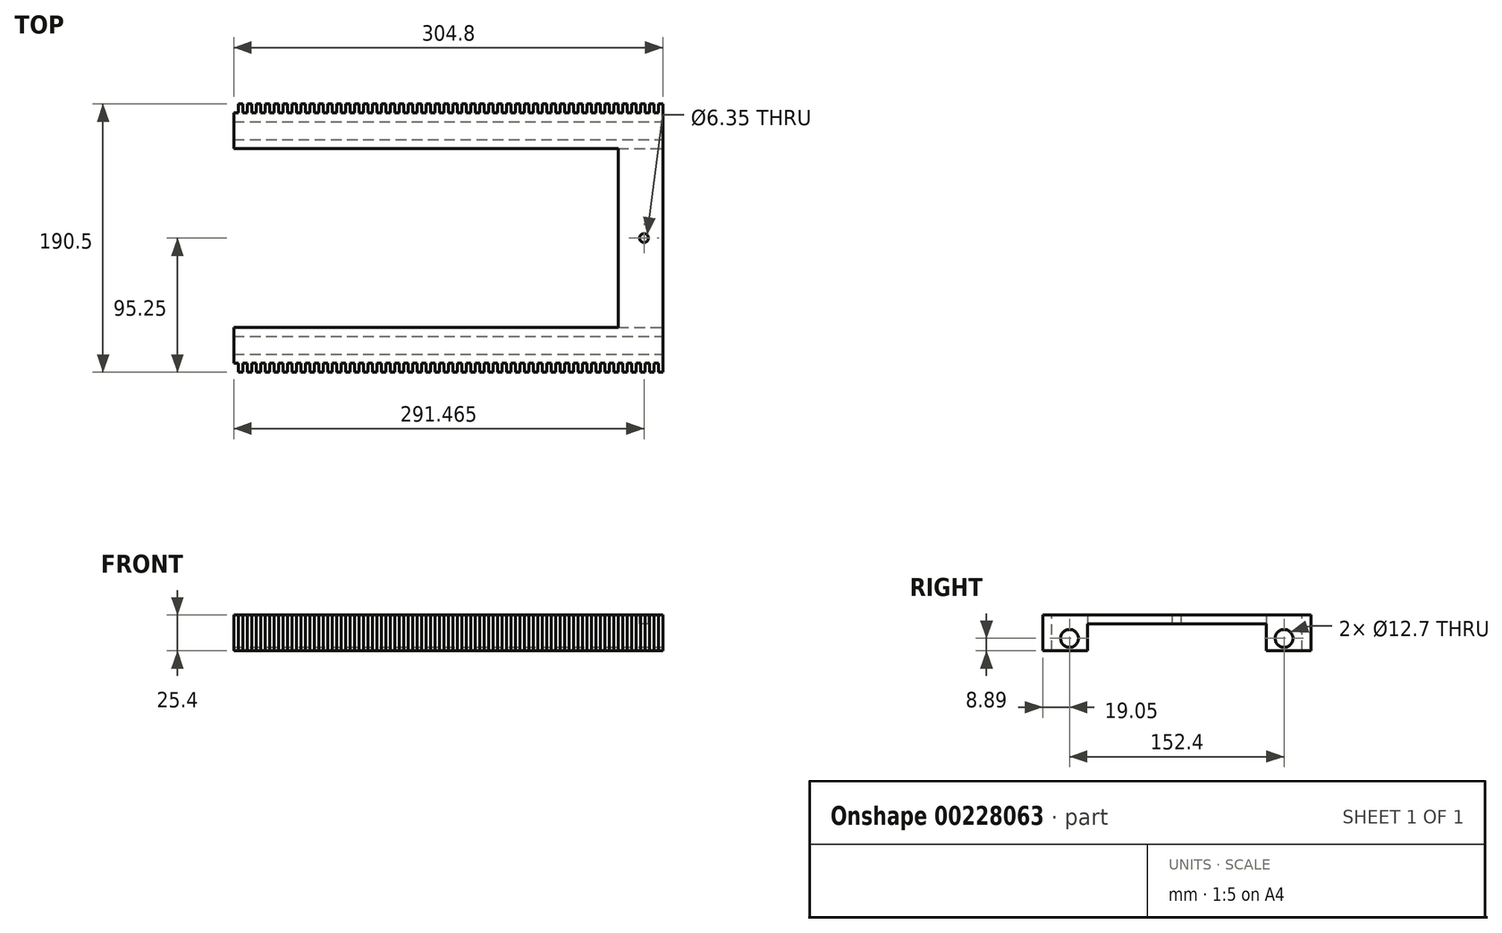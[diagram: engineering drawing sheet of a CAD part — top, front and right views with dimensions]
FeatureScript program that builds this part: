
annotation { "Feature Type Name" : "Feature", "Feature Type Description" : "" }
export const myFeature = defineFeature(function(context is Context, id is Id, definition is map)
    precondition{}
    {
        {
            var Q0;
            Q0=qCreatedBy(makeId("Top.planeOp"),FACE);
            var sketch = newSketch(context, id + "F0", { "sketchPlane" : qUnion([Q0])});
            skLineSegment(sketch, "E0.bottom", {"start": v(0, 0) * mm, "end": v(304.8, 0) * mm});
            skLineSegment(sketch, "E0.top", {"start": v(0, 190.5) * mm, "end": v(304.8, 190.5) * mm});
            skLineSegment(sketch, "E0.left", {"start": v(0, 0) * mm, "end": v(0, 190.5) * mm});
            skLineSegment(sketch, "E0.right", {"start": v(304.8, 0) * mm, "end": v(304.8, 190.5) * mm});
            skLineSegment(sketch, "E1.bottom", {"start": v(6.35, 158.75) * mm, "end": v(273.05, 158.75) * mm});
            skLineSegment(sketch, "E1.top", {"start": v(6.35, 31.75) * mm, "end": v(273.05, 31.75) * mm});
            skLineSegment(sketch, "E1.left", {"start": v(6.35, 158.75) * mm, "end": v(6.35, 31.75) * mm});
            skLineSegment(sketch, "E1.right", {"start": v(273.05, 158.75) * mm, "end": v(273.05, 31.75) * mm});
            skLineSegment(sketch, "E2", {"start": v(0, 190.5) * mm, "end": v(6.35, 158.75) * mm, "construction": true});
            skLineSegment(sketch, "E3", {"start": v(6.35, 31.75) * mm, "end": v(0, 0) * mm, "construction": true});
            skSolve(sketch);
        }
        {
            var Q0;
            Q0 = qSketchRegion(id + "F0", true);
            extrude(context, id + "F1", {"entities" : qUnion([Q0]), "depth" : 6.35 * mm, "offsetDistance" : 25.4 * mm});
        }
        {
            var Q0;
            Q0=makeQuery(id+"F1.opExtrude","SWEPT_FACE",FACE,{"disambiguationData":[OSD([sQuery(id+"F0.wireOp",EDGE,"E0.right")])]});
            var sketch = newSketch(context, id + "F2", { "sketchPlane" : qUnion([Q0])});
            skLineSegment(sketch, "E4.bottom", {"start": v(0, 0) * mm, "end": v(31.75, 0) * mm});
            skLineSegment(sketch, "E4.top", {"start": v(0, -19.05) * mm, "end": v(31.75, -19.05) * mm});
            skLineSegment(sketch, "E4.left", {"start": v(0, 0) * mm, "end": v(0, -19.05) * mm});
            skLineSegment(sketch, "E4.right", {"start": v(31.75, 0) * mm, "end": v(31.75, -19.05) * mm});
            skLineSegment(sketch, "E5.bottom", {"start": v(190.5, 0) * mm, "end": v(158.75, 0) * mm});
            skLineSegment(sketch, "E5.top", {"start": v(190.5, -19.05) * mm, "end": v(158.75, -19.05) * mm});
            skLineSegment(sketch, "E5.left", {"start": v(190.5, 0) * mm, "end": v(190.5, -19.05) * mm});
            skLineSegment(sketch, "E5.right", {"start": v(158.75, 0) * mm, "end": v(158.75, -19.05) * mm});
            skCircle(sketch, "E6", {"center": v(19.05, -10.16) * mm, "radius": 6.35 * mm});
            skCircle(sketch, "E7", {"center": v(171.45, -10.16) * mm, "radius": 6.35 * mm});
            skLineSegment(sketch, "E8", {"start": v(19.05, -10.16) * mm, "end": v(0, 0) * mm, "construction": true});
            skLineSegment(sketch, "E9", {"start": v(171.45, -10.16) * mm, "end": v(190.5, 0) * mm, "construction": true});
            skSolve(sketch);
        }
        {
            var Q0;
            Q0 = qSketchRegion(id + "F2", true);
            var Q1;
            Q1=makeQuery(id+"F1.opExtrude","SWEPT_FACE",FACE,{"disambiguationData":[OSD([sQuery(id+"F0.wireOp",EDGE,"E0.left")])]});
            extrude(context, id + "F3", {"entities" : qUnion([Q0]), "operationType" : NewBodyOperationType.ADD, "endBound" : BoundingType.UP_TO_SURFACE, "oppositeDirection" : true, "depth" : 25.4 * mm, "endBoundEntityFace" : qUnion([Q1]), "offsetDistance" : 25.4 * mm});
        }
        {
            var Q0;
            Q0=makeQuery(id+"F1.opExtrude","CAP_FACE",FACE,{"disambiguationData":[OSD([sQuery(id+"F0.wireOp",EDGE,"E0.bottom"),sQuery(id+"F0.wireOp",EDGE,"E0.top"),sQuery(id+"F0.wireOp",EDGE,"E0.left"),sQuery(id+"F0.wireOp",EDGE,"E0.right"),sQuery(id+"F0.wireOp",EDGE,"E1.bottom"),sQuery(id+"F0.wireOp",EDGE,"E1.top"),sQuery(id+"F0.wireOp",EDGE,"E1.left"),sQuery(id+"F0.wireOp",EDGE,"E1.right")])],"isStart":false});
            var sketch = newSketch(context, id + "F4", { "sketchPlane" : qUnion([Q0])});
            skLineSegment(sketch, "E10.bottom", {"start": v(0, 190.5) * mm, "end": v(3.18, 190.5) * mm});
            skLineSegment(sketch, "E10.top", {"start": v(0, 184.15) * mm, "end": v(3.18, 184.15) * mm});
            skLineSegment(sketch, "E10.left", {"start": v(0, 190.5) * mm, "end": v(0, 184.15) * mm});
            skLineSegment(sketch, "E10.right", {"start": v(3.18, 190.5) * mm, "end": v(3.18, 184.15) * mm});
            skLineSegment(sketch, "E11", {"start": v(0, 95.25) * mm, "end": v(304.8, 95.25) * mm, "construction": true});
            skLineSegment(sketch, "E12.1.0.0", {"start": v(6.35, 190.5) * mm, "end": v(9.53, 190.5) * mm});
            skLineSegment(sketch, "E12.1.0.1", {"start": v(6.35, 184.15) * mm, "end": v(9.53, 184.15) * mm});
            skLineSegment(sketch, "E12.1.0.2", {"start": v(6.35, 190.5) * mm, "end": v(6.35, 184.15) * mm});
            skLineSegment(sketch, "E12.1.0.3", {"start": v(9.53, 190.5) * mm, "end": v(9.53, 184.15) * mm});
            skLineSegment(sketch, "E12.2.0.0", {"start": v(12.7, 190.5) * mm, "end": v(15.88, 190.5) * mm});
            skLineSegment(sketch, "E12.2.0.1", {"start": v(12.7, 184.15) * mm, "end": v(15.88, 184.15) * mm});
            skLineSegment(sketch, "E12.2.0.2", {"start": v(12.7, 190.5) * mm, "end": v(12.7, 184.15) * mm});
            skLineSegment(sketch, "E12.2.0.3", {"start": v(15.88, 190.5) * mm, "end": v(15.88, 184.15) * mm});
            skLineSegment(sketch, "E12.3.0.0", {"start": v(19.05, 190.5) * mm, "end": v(22.23, 190.5) * mm});
            skLineSegment(sketch, "E12.3.0.1", {"start": v(19.05, 184.15) * mm, "end": v(22.23, 184.15) * mm});
            skLineSegment(sketch, "E12.3.0.2", {"start": v(19.05, 190.5) * mm, "end": v(19.05, 184.15) * mm});
            skLineSegment(sketch, "E12.3.0.3", {"start": v(22.23, 190.5) * mm, "end": v(22.23, 184.15) * mm});
            skLineSegment(sketch, "E12.4.0.0", {"start": v(25.4, 190.5) * mm, "end": v(28.58, 190.5) * mm});
            skLineSegment(sketch, "E12.4.0.1", {"start": v(25.4, 184.15) * mm, "end": v(28.58, 184.15) * mm});
            skLineSegment(sketch, "E12.4.0.2", {"start": v(25.4, 190.5) * mm, "end": v(25.4, 184.15) * mm});
            skLineSegment(sketch, "E12.4.0.3", {"start": v(28.58, 190.5) * mm, "end": v(28.58, 184.15) * mm});
            skLineSegment(sketch, "E12.5.0.0", {"start": v(31.75, 190.5) * mm, "end": v(34.93, 190.5) * mm});
            skLineSegment(sketch, "E12.5.0.1", {"start": v(31.75, 184.15) * mm, "end": v(34.93, 184.15) * mm});
            skLineSegment(sketch, "E12.5.0.2", {"start": v(31.75, 190.5) * mm, "end": v(31.75, 184.15) * mm});
            skLineSegment(sketch, "E12.5.0.3", {"start": v(34.93, 190.5) * mm, "end": v(34.93, 184.15) * mm});
            skLineSegment(sketch, "E12.6.0.0", {"start": v(38.1, 190.5) * mm, "end": v(41.28, 190.5) * mm});
            skLineSegment(sketch, "E12.6.0.1", {"start": v(38.1, 184.15) * mm, "end": v(41.28, 184.15) * mm});
            skLineSegment(sketch, "E12.6.0.2", {"start": v(38.1, 190.5) * mm, "end": v(38.1, 184.15) * mm});
            skLineSegment(sketch, "E12.6.0.3", {"start": v(41.28, 190.5) * mm, "end": v(41.28, 184.15) * mm});
            skLineSegment(sketch, "E12.7.0.0", {"start": v(44.45, 190.5) * mm, "end": v(47.63, 190.5) * mm});
            skLineSegment(sketch, "E12.7.0.1", {"start": v(44.45, 184.15) * mm, "end": v(47.63, 184.15) * mm});
            skLineSegment(sketch, "E12.7.0.2", {"start": v(44.45, 190.5) * mm, "end": v(44.45, 184.15) * mm});
            skLineSegment(sketch, "E12.7.0.3", {"start": v(47.63, 190.5) * mm, "end": v(47.63, 184.15) * mm});
            skLineSegment(sketch, "E12.8.0.0", {"start": v(50.8, 190.5) * mm, "end": v(53.98, 190.5) * mm});
            skLineSegment(sketch, "E12.8.0.1", {"start": v(50.8, 184.15) * mm, "end": v(53.98, 184.15) * mm});
            skLineSegment(sketch, "E12.8.0.2", {"start": v(50.8, 190.5) * mm, "end": v(50.8, 184.15) * mm});
            skLineSegment(sketch, "E12.8.0.3", {"start": v(53.98, 190.5) * mm, "end": v(53.98, 184.15) * mm});
            skLineSegment(sketch, "E12.9.0.0", {"start": v(57.15, 190.5) * mm, "end": v(60.33, 190.5) * mm});
            skLineSegment(sketch, "E12.9.0.1", {"start": v(57.15, 184.15) * mm, "end": v(60.33, 184.15) * mm});
            skLineSegment(sketch, "E12.9.0.2", {"start": v(57.15, 190.5) * mm, "end": v(57.15, 184.15) * mm});
            skLineSegment(sketch, "E12.9.0.3", {"start": v(60.33, 190.5) * mm, "end": v(60.33, 184.15) * mm});
            skLineSegment(sketch, "E12.10.0.0", {"start": v(63.5, 190.5) * mm, "end": v(66.68, 190.5) * mm});
            skLineSegment(sketch, "E12.10.0.1", {"start": v(63.5, 184.15) * mm, "end": v(66.68, 184.15) * mm});
            skLineSegment(sketch, "E12.10.0.2", {"start": v(63.5, 190.5) * mm, "end": v(63.5, 184.15) * mm});
            skLineSegment(sketch, "E12.10.0.3", {"start": v(66.68, 190.5) * mm, "end": v(66.68, 184.15) * mm});
            skLineSegment(sketch, "E12.11.0.0", {"start": v(69.85, 190.5) * mm, "end": v(73.03, 190.5) * mm});
            skLineSegment(sketch, "E12.11.0.1", {"start": v(69.85, 184.15) * mm, "end": v(73.03, 184.15) * mm});
            skLineSegment(sketch, "E12.11.0.2", {"start": v(69.85, 190.5) * mm, "end": v(69.85, 184.15) * mm});
            skLineSegment(sketch, "E12.11.0.3", {"start": v(73.03, 190.5) * mm, "end": v(73.03, 184.15) * mm});
            skLineSegment(sketch, "E12.12.0.0", {"start": v(76.2, 190.5) * mm, "end": v(79.38, 190.5) * mm});
            skLineSegment(sketch, "E12.12.0.1", {"start": v(76.2, 184.15) * mm, "end": v(79.38, 184.15) * mm});
            skLineSegment(sketch, "E12.12.0.2", {"start": v(76.2, 190.5) * mm, "end": v(76.2, 184.15) * mm});
            skLineSegment(sketch, "E12.12.0.3", {"start": v(79.38, 190.5) * mm, "end": v(79.38, 184.15) * mm});
            skLineSegment(sketch, "E12.13.0.0", {"start": v(82.55, 190.5) * mm, "end": v(85.73, 190.5) * mm});
            skLineSegment(sketch, "E12.13.0.1", {"start": v(82.55, 184.15) * mm, "end": v(85.73, 184.15) * mm});
            skLineSegment(sketch, "E12.13.0.2", {"start": v(82.55, 190.5) * mm, "end": v(82.55, 184.15) * mm});
            skLineSegment(sketch, "E12.13.0.3", {"start": v(85.73, 190.5) * mm, "end": v(85.73, 184.15) * mm});
            skLineSegment(sketch, "E12.14.0.0", {"start": v(88.9, 190.5) * mm, "end": v(92.08, 190.5) * mm});
            skLineSegment(sketch, "E12.14.0.1", {"start": v(88.9, 184.15) * mm, "end": v(92.08, 184.15) * mm});
            skLineSegment(sketch, "E12.14.0.2", {"start": v(88.9, 190.5) * mm, "end": v(88.9, 184.15) * mm});
            skLineSegment(sketch, "E12.14.0.3", {"start": v(92.08, 190.5) * mm, "end": v(92.08, 184.15) * mm});
            skLineSegment(sketch, "E12.15.0.0", {"start": v(95.25, 190.5) * mm, "end": v(98.43, 190.5) * mm});
            skLineSegment(sketch, "E12.15.0.1", {"start": v(95.25, 184.15) * mm, "end": v(98.43, 184.15) * mm});
            skLineSegment(sketch, "E12.15.0.2", {"start": v(95.25, 190.5) * mm, "end": v(95.25, 184.15) * mm});
            skLineSegment(sketch, "E12.15.0.3", {"start": v(98.43, 190.5) * mm, "end": v(98.43, 184.15) * mm});
            skLineSegment(sketch, "E12.16.0.0", {"start": v(101.6, 190.5) * mm, "end": v(104.78, 190.5) * mm});
            skLineSegment(sketch, "E12.16.0.1", {"start": v(101.6, 184.15) * mm, "end": v(104.78, 184.15) * mm});
            skLineSegment(sketch, "E12.16.0.2", {"start": v(101.6, 190.5) * mm, "end": v(101.6, 184.15) * mm});
            skLineSegment(sketch, "E12.16.0.3", {"start": v(104.78, 190.5) * mm, "end": v(104.78, 184.15) * mm});
            skLineSegment(sketch, "E12.17.0.0", {"start": v(107.95, 190.5) * mm, "end": v(111.13, 190.5) * mm});
            skLineSegment(sketch, "E12.17.0.1", {"start": v(107.95, 184.15) * mm, "end": v(111.13, 184.15) * mm});
            skLineSegment(sketch, "E12.17.0.2", {"start": v(107.95, 190.5) * mm, "end": v(107.95, 184.15) * mm});
            skLineSegment(sketch, "E12.17.0.3", {"start": v(111.13, 190.5) * mm, "end": v(111.13, 184.15) * mm});
            skLineSegment(sketch, "E12.18.0.0", {"start": v(114.3, 190.5) * mm, "end": v(117.48, 190.5) * mm});
            skLineSegment(sketch, "E12.18.0.1", {"start": v(114.3, 184.15) * mm, "end": v(117.48, 184.15) * mm});
            skLineSegment(sketch, "E12.18.0.2", {"start": v(114.3, 190.5) * mm, "end": v(114.3, 184.15) * mm});
            skLineSegment(sketch, "E12.18.0.3", {"start": v(117.48, 190.5) * mm, "end": v(117.48, 184.15) * mm});
            skLineSegment(sketch, "E12.19.0.0", {"start": v(120.65, 190.5) * mm, "end": v(123.83, 190.5) * mm});
            skLineSegment(sketch, "E12.19.0.1", {"start": v(120.65, 184.15) * mm, "end": v(123.83, 184.15) * mm});
            skLineSegment(sketch, "E12.19.0.2", {"start": v(120.65, 190.5) * mm, "end": v(120.65, 184.15) * mm});
            skLineSegment(sketch, "E12.19.0.3", {"start": v(123.83, 190.5) * mm, "end": v(123.83, 184.15) * mm});
            skLineSegment(sketch, "E12.20.0.0", {"start": v(127, 190.5) * mm, "end": v(130.18, 190.5) * mm});
            skLineSegment(sketch, "E12.20.0.1", {"start": v(127, 184.15) * mm, "end": v(130.18, 184.15) * mm});
            skLineSegment(sketch, "E12.20.0.2", {"start": v(127, 190.5) * mm, "end": v(127, 184.15) * mm});
            skLineSegment(sketch, "E12.20.0.3", {"start": v(130.18, 190.5) * mm, "end": v(130.18, 184.15) * mm});
            skLineSegment(sketch, "E12.21.0.0", {"start": v(133.35, 190.5) * mm, "end": v(136.53, 190.5) * mm});
            skLineSegment(sketch, "E12.21.0.1", {"start": v(133.35, 184.15) * mm, "end": v(136.53, 184.15) * mm});
            skLineSegment(sketch, "E12.21.0.2", {"start": v(133.35, 190.5) * mm, "end": v(133.35, 184.15) * mm});
            skLineSegment(sketch, "E12.21.0.3", {"start": v(136.53, 190.5) * mm, "end": v(136.53, 184.15) * mm});
            skLineSegment(sketch, "E12.22.0.0", {"start": v(139.7, 190.5) * mm, "end": v(142.88, 190.5) * mm});
            skLineSegment(sketch, "E12.22.0.1", {"start": v(139.7, 184.15) * mm, "end": v(142.88, 184.15) * mm});
            skLineSegment(sketch, "E12.22.0.2", {"start": v(139.7, 190.5) * mm, "end": v(139.7, 184.15) * mm});
            skLineSegment(sketch, "E12.22.0.3", {"start": v(142.88, 190.5) * mm, "end": v(142.88, 184.15) * mm});
            skLineSegment(sketch, "E12.23.0.0", {"start": v(146.05, 190.5) * mm, "end": v(149.23, 190.5) * mm});
            skLineSegment(sketch, "E12.23.0.1", {"start": v(146.05, 184.15) * mm, "end": v(149.23, 184.15) * mm});
            skLineSegment(sketch, "E12.23.0.2", {"start": v(146.05, 190.5) * mm, "end": v(146.05, 184.15) * mm});
            skLineSegment(sketch, "E12.23.0.3", {"start": v(149.23, 190.5) * mm, "end": v(149.23, 184.15) * mm});
            skLineSegment(sketch, "E12.24.0.0", {"start": v(152.4, 190.5) * mm, "end": v(155.58, 190.5) * mm});
            skLineSegment(sketch, "E12.24.0.1", {"start": v(152.4, 184.15) * mm, "end": v(155.58, 184.15) * mm});
            skLineSegment(sketch, "E12.24.0.2", {"start": v(152.4, 190.5) * mm, "end": v(152.4, 184.15) * mm});
            skLineSegment(sketch, "E12.24.0.3", {"start": v(155.58, 190.5) * mm, "end": v(155.58, 184.15) * mm});
            skLineSegment(sketch, "E12.25.0.0", {"start": v(158.75, 190.5) * mm, "end": v(161.93, 190.5) * mm});
            skLineSegment(sketch, "E12.25.0.1", {"start": v(158.75, 184.15) * mm, "end": v(161.93, 184.15) * mm});
            skLineSegment(sketch, "E12.25.0.2", {"start": v(158.75, 190.5) * mm, "end": v(158.75, 184.15) * mm});
            skLineSegment(sketch, "E12.25.0.3", {"start": v(161.93, 190.5) * mm, "end": v(161.93, 184.15) * mm});
            skLineSegment(sketch, "E12.26.0.0", {"start": v(165.1, 190.5) * mm, "end": v(168.28, 190.5) * mm});
            skLineSegment(sketch, "E12.26.0.1", {"start": v(165.1, 184.15) * mm, "end": v(168.28, 184.15) * mm});
            skLineSegment(sketch, "E12.26.0.2", {"start": v(165.1, 190.5) * mm, "end": v(165.1, 184.15) * mm});
            skLineSegment(sketch, "E12.26.0.3", {"start": v(168.28, 190.5) * mm, "end": v(168.28, 184.15) * mm});
            skLineSegment(sketch, "E12.27.0.0", {"start": v(171.45, 190.5) * mm, "end": v(174.63, 190.5) * mm});
            skLineSegment(sketch, "E12.27.0.1", {"start": v(171.45, 184.15) * mm, "end": v(174.63, 184.15) * mm});
            skLineSegment(sketch, "E12.27.0.2", {"start": v(171.45, 190.5) * mm, "end": v(171.45, 184.15) * mm});
            skLineSegment(sketch, "E12.27.0.3", {"start": v(174.63, 190.5) * mm, "end": v(174.63, 184.15) * mm});
            skLineSegment(sketch, "E12.28.0.0", {"start": v(177.8, 190.5) * mm, "end": v(180.98, 190.5) * mm});
            skLineSegment(sketch, "E12.28.0.1", {"start": v(177.8, 184.15) * mm, "end": v(180.98, 184.15) * mm});
            skLineSegment(sketch, "E12.28.0.2", {"start": v(177.8, 190.5) * mm, "end": v(177.8, 184.15) * mm});
            skLineSegment(sketch, "E12.28.0.3", {"start": v(180.98, 190.5) * mm, "end": v(180.98, 184.15) * mm});
            skLineSegment(sketch, "E12.29.0.0", {"start": v(184.15, 190.5) * mm, "end": v(187.33, 190.5) * mm});
            skLineSegment(sketch, "E12.29.0.1", {"start": v(184.15, 184.15) * mm, "end": v(187.33, 184.15) * mm});
            skLineSegment(sketch, "E12.29.0.2", {"start": v(184.15, 190.5) * mm, "end": v(184.15, 184.15) * mm});
            skLineSegment(sketch, "E12.29.0.3", {"start": v(187.33, 190.5) * mm, "end": v(187.33, 184.15) * mm});
            skLineSegment(sketch, "E12.30.0.0", {"start": v(190.5, 190.5) * mm, "end": v(193.68, 190.5) * mm});
            skLineSegment(sketch, "E12.30.0.1", {"start": v(190.5, 184.15) * mm, "end": v(193.68, 184.15) * mm});
            skLineSegment(sketch, "E12.30.0.2", {"start": v(190.5, 190.5) * mm, "end": v(190.5, 184.15) * mm});
            skLineSegment(sketch, "E12.30.0.3", {"start": v(193.68, 190.5) * mm, "end": v(193.68, 184.15) * mm});
            skLineSegment(sketch, "E12.31.0.0", {"start": v(196.85, 190.5) * mm, "end": v(200.03, 190.5) * mm});
            skLineSegment(sketch, "E12.31.0.1", {"start": v(196.85, 184.15) * mm, "end": v(200.03, 184.15) * mm});
            skLineSegment(sketch, "E12.31.0.2", {"start": v(196.85, 190.5) * mm, "end": v(196.85, 184.15) * mm});
            skLineSegment(sketch, "E12.31.0.3", {"start": v(200.03, 190.5) * mm, "end": v(200.03, 184.15) * mm});
            skLineSegment(sketch, "E12.32.0.0", {"start": v(203.2, 190.5) * mm, "end": v(206.38, 190.5) * mm});
            skLineSegment(sketch, "E12.32.0.1", {"start": v(203.2, 184.15) * mm, "end": v(206.38, 184.15) * mm});
            skLineSegment(sketch, "E12.32.0.2", {"start": v(203.2, 190.5) * mm, "end": v(203.2, 184.15) * mm});
            skLineSegment(sketch, "E12.32.0.3", {"start": v(206.38, 190.5) * mm, "end": v(206.38, 184.15) * mm});
            skLineSegment(sketch, "E12.33.0.0", {"start": v(209.55, 190.5) * mm, "end": v(212.73, 190.5) * mm});
            skLineSegment(sketch, "E12.33.0.1", {"start": v(209.55, 184.15) * mm, "end": v(212.73, 184.15) * mm});
            skLineSegment(sketch, "E12.33.0.2", {"start": v(209.55, 190.5) * mm, "end": v(209.55, 184.15) * mm});
            skLineSegment(sketch, "E12.33.0.3", {"start": v(212.73, 190.5) * mm, "end": v(212.73, 184.15) * mm});
            skLineSegment(sketch, "E12.34.0.0", {"start": v(215.9, 190.5) * mm, "end": v(219.08, 190.5) * mm});
            skLineSegment(sketch, "E12.34.0.1", {"start": v(215.9, 184.15) * mm, "end": v(219.08, 184.15) * mm});
            skLineSegment(sketch, "E12.34.0.2", {"start": v(215.9, 190.5) * mm, "end": v(215.9, 184.15) * mm});
            skLineSegment(sketch, "E12.34.0.3", {"start": v(219.08, 190.5) * mm, "end": v(219.08, 184.15) * mm});
            skLineSegment(sketch, "E12.35.0.0", {"start": v(222.25, 190.5) * mm, "end": v(225.43, 190.5) * mm});
            skLineSegment(sketch, "E12.35.0.1", {"start": v(222.25, 184.15) * mm, "end": v(225.43, 184.15) * mm});
            skLineSegment(sketch, "E12.35.0.2", {"start": v(222.25, 190.5) * mm, "end": v(222.25, 184.15) * mm});
            skLineSegment(sketch, "E12.35.0.3", {"start": v(225.43, 190.5) * mm, "end": v(225.43, 184.15) * mm});
            skLineSegment(sketch, "E12.36.0.0", {"start": v(228.6, 190.5) * mm, "end": v(231.78, 190.5) * mm});
            skLineSegment(sketch, "E12.36.0.1", {"start": v(228.6, 184.15) * mm, "end": v(231.78, 184.15) * mm});
            skLineSegment(sketch, "E12.36.0.2", {"start": v(228.6, 190.5) * mm, "end": v(228.6, 184.15) * mm});
            skLineSegment(sketch, "E12.36.0.3", {"start": v(231.78, 190.5) * mm, "end": v(231.78, 184.15) * mm});
            skLineSegment(sketch, "E12.37.0.0", {"start": v(234.95, 190.5) * mm, "end": v(238.13, 190.5) * mm});
            skLineSegment(sketch, "E12.37.0.1", {"start": v(234.95, 184.15) * mm, "end": v(238.13, 184.15) * mm});
            skLineSegment(sketch, "E12.37.0.2", {"start": v(234.95, 190.5) * mm, "end": v(234.95, 184.15) * mm});
            skLineSegment(sketch, "E12.37.0.3", {"start": v(238.13, 190.5) * mm, "end": v(238.13, 184.15) * mm});
            skLineSegment(sketch, "E12.38.0.0", {"start": v(241.3, 190.5) * mm, "end": v(244.48, 190.5) * mm});
            skLineSegment(sketch, "E12.38.0.1", {"start": v(241.3, 184.15) * mm, "end": v(244.48, 184.15) * mm});
            skLineSegment(sketch, "E12.38.0.2", {"start": v(241.3, 190.5) * mm, "end": v(241.3, 184.15) * mm});
            skLineSegment(sketch, "E12.38.0.3", {"start": v(244.48, 190.5) * mm, "end": v(244.48, 184.15) * mm});
            skLineSegment(sketch, "E12.39.0.0", {"start": v(247.65, 190.5) * mm, "end": v(250.83, 190.5) * mm});
            skLineSegment(sketch, "E12.39.0.1", {"start": v(247.65, 184.15) * mm, "end": v(250.83, 184.15) * mm});
            skLineSegment(sketch, "E12.39.0.2", {"start": v(247.65, 190.5) * mm, "end": v(247.65, 184.15) * mm});
            skLineSegment(sketch, "E12.39.0.3", {"start": v(250.83, 190.5) * mm, "end": v(250.83, 184.15) * mm});
            skLineSegment(sketch, "E12.40.0.0", {"start": v(254, 190.5) * mm, "end": v(257.18, 190.5) * mm});
            skLineSegment(sketch, "E12.40.0.1", {"start": v(254, 184.15) * mm, "end": v(257.18, 184.15) * mm});
            skLineSegment(sketch, "E12.40.0.2", {"start": v(254, 190.5) * mm, "end": v(254, 184.15) * mm});
            skLineSegment(sketch, "E12.40.0.3", {"start": v(257.18, 190.5) * mm, "end": v(257.18, 184.15) * mm});
            skLineSegment(sketch, "E12.41.0.0", {"start": v(260.35, 190.5) * mm, "end": v(263.53, 190.5) * mm});
            skLineSegment(sketch, "E12.41.0.1", {"start": v(260.35, 184.15) * mm, "end": v(263.53, 184.15) * mm});
            skLineSegment(sketch, "E12.41.0.2", {"start": v(260.35, 190.5) * mm, "end": v(260.35, 184.15) * mm});
            skLineSegment(sketch, "E12.41.0.3", {"start": v(263.53, 190.5) * mm, "end": v(263.53, 184.15) * mm});
            skLineSegment(sketch, "E12.42.0.0", {"start": v(266.7, 190.5) * mm, "end": v(269.88, 190.5) * mm});
            skLineSegment(sketch, "E12.42.0.1", {"start": v(266.7, 184.15) * mm, "end": v(269.88, 184.15) * mm});
            skLineSegment(sketch, "E12.42.0.2", {"start": v(266.7, 190.5) * mm, "end": v(266.7, 184.15) * mm});
            skLineSegment(sketch, "E12.42.0.3", {"start": v(269.88, 190.5) * mm, "end": v(269.88, 184.15) * mm});
            skLineSegment(sketch, "E12.43.0.0", {"start": v(273.05, 190.5) * mm, "end": v(276.23, 190.5) * mm});
            skLineSegment(sketch, "E12.43.0.1", {"start": v(273.05, 184.15) * mm, "end": v(276.23, 184.15) * mm});
            skLineSegment(sketch, "E12.43.0.2", {"start": v(273.05, 190.5) * mm, "end": v(273.05, 184.15) * mm});
            skLineSegment(sketch, "E12.43.0.3", {"start": v(276.23, 190.5) * mm, "end": v(276.23, 184.15) * mm});
            skLineSegment(sketch, "E12.44.0.0", {"start": v(279.4, 190.5) * mm, "end": v(282.58, 190.5) * mm});
            skLineSegment(sketch, "E12.44.0.1", {"start": v(279.4, 184.15) * mm, "end": v(282.58, 184.15) * mm});
            skLineSegment(sketch, "E12.44.0.2", {"start": v(279.4, 190.5) * mm, "end": v(279.4, 184.15) * mm});
            skLineSegment(sketch, "E12.44.0.3", {"start": v(282.58, 190.5) * mm, "end": v(282.58, 184.15) * mm});
            skLineSegment(sketch, "E12.45.0.0", {"start": v(285.75, 190.5) * mm, "end": v(288.93, 190.5) * mm});
            skLineSegment(sketch, "E12.45.0.1", {"start": v(285.75, 184.15) * mm, "end": v(288.93, 184.15) * mm});
            skLineSegment(sketch, "E12.45.0.2", {"start": v(285.75, 190.5) * mm, "end": v(285.75, 184.15) * mm});
            skLineSegment(sketch, "E12.45.0.3", {"start": v(288.93, 190.5) * mm, "end": v(288.93, 184.15) * mm});
            skLineSegment(sketch, "E12.46.0.0", {"start": v(292.1, 190.5) * mm, "end": v(295.28, 190.5) * mm});
            skLineSegment(sketch, "E12.46.0.1", {"start": v(292.1, 184.15) * mm, "end": v(295.28, 184.15) * mm});
            skLineSegment(sketch, "E12.46.0.2", {"start": v(292.1, 190.5) * mm, "end": v(292.1, 184.15) * mm});
            skLineSegment(sketch, "E12.46.0.3", {"start": v(295.28, 190.5) * mm, "end": v(295.28, 184.15) * mm});
            skLineSegment(sketch, "E12.47.0.0", {"start": v(298.45, 190.5) * mm, "end": v(301.63, 190.5) * mm});
            skLineSegment(sketch, "E12.47.0.1", {"start": v(298.45, 184.15) * mm, "end": v(301.63, 184.15) * mm});
            skLineSegment(sketch, "E12.47.0.2", {"start": v(298.45, 190.5) * mm, "end": v(298.45, 184.15) * mm});
            skLineSegment(sketch, "E12.47.0.3", {"start": v(301.63, 190.5) * mm, "end": v(301.63, 184.15) * mm});
            skLineSegment(sketch, "E12.direction1", {"start": v(0, 184.15) * mm, "end": v(6.35, 184.15) * mm, "construction": true});
            skLineSegment(sketch, "E13.MirrorCS", {"start": v(63.5, 0) * mm, "end": v(66.68, 0) * mm});
            skLineSegment(sketch, "E14.MirrorCS", {"start": v(88.9, 0) * mm, "end": v(92.08, 0) * mm});
            skLineSegment(sketch, "E15.MirrorCS", {"start": v(82.55, 0) * mm, "end": v(85.73, 0) * mm});
            skLineSegment(sketch, "E16.MirrorCS", {"start": v(57.15, 0) * mm, "end": v(60.33, 0) * mm});
            skLineSegment(sketch, "E17.MirrorCS", {"start": v(50.8, 0) * mm, "end": v(53.98, 0) * mm});
            skLineSegment(sketch, "E18.MirrorCS", {"start": v(76.2, 0) * mm, "end": v(79.38, 0) * mm});
            skLineSegment(sketch, "E19.MirrorCS", {"start": v(171.45, 6.35) * mm, "end": v(174.63, 6.35) * mm});
            skLineSegment(sketch, "E20.MirrorCS", {"start": v(196.85, 6.35) * mm, "end": v(200.03, 6.35) * mm});
            skLineSegment(sketch, "E21.MirrorCS", {"start": v(222.25, 6.35) * mm, "end": v(225.43, 6.35) * mm});
            skLineSegment(sketch, "E22.MirrorCS", {"start": v(69.85, 6.35) * mm, "end": v(73.03, 6.35) * mm});
            skLineSegment(sketch, "E23.MirrorCS", {"start": v(95.25, 6.35) * mm, "end": v(98.43, 6.35) * mm});
            skLineSegment(sketch, "E24.MirrorCS", {"start": v(120.65, 6.35) * mm, "end": v(123.83, 6.35) * mm});
            skLineSegment(sketch, "E25.MirrorCS", {"start": v(146.05, 6.35) * mm, "end": v(149.23, 6.35) * mm});
            skLineSegment(sketch, "E26.MirrorCS", {"start": v(44.45, 6.35) * mm, "end": v(47.63, 6.35) * mm});
            skLineSegment(sketch, "E27.MirrorCS", {"start": v(244.48, 0) * mm, "end": v(244.48, 6.35) * mm});
            skLineSegment(sketch, "E28.MirrorCS", {"start": v(142.88, 0) * mm, "end": v(142.88, 6.35) * mm});
            skLineSegment(sketch, "E29.MirrorCS", {"start": v(168.28, 0) * mm, "end": v(168.28, 6.35) * mm});
            skLineSegment(sketch, "E30.MirrorCS", {"start": v(193.68, 0) * mm, "end": v(193.68, 6.35) * mm});
            skLineSegment(sketch, "E31.MirrorCS", {"start": v(219.08, 0) * mm, "end": v(219.08, 6.35) * mm});
            skLineSegment(sketch, "E32.MirrorCS", {"start": v(66.68, 0) * mm, "end": v(66.68, 6.35) * mm});
            skLineSegment(sketch, "E33.MirrorCS", {"start": v(92.08, 0) * mm, "end": v(92.08, 6.35) * mm});
            skLineSegment(sketch, "E34.MirrorCS", {"start": v(117.48, 0) * mm, "end": v(117.48, 6.35) * mm});
            skLineSegment(sketch, "E35.MirrorCS", {"start": v(171.45, 0) * mm, "end": v(174.63, 0) * mm});
            skLineSegment(sketch, "E36.MirrorCS", {"start": v(196.85, 0) * mm, "end": v(200.03, 0) * mm});
            skLineSegment(sketch, "E37.MirrorCS", {"start": v(222.25, 0) * mm, "end": v(225.43, 0) * mm});
            skLineSegment(sketch, "E38.MirrorCS", {"start": v(247.65, 0) * mm, "end": v(250.83, 0) * mm});
            skLineSegment(sketch, "E39.MirrorCS", {"start": v(69.85, 0) * mm, "end": v(73.03, 0) * mm});
            skLineSegment(sketch, "E40.MirrorCS", {"start": v(95.25, 0) * mm, "end": v(98.43, 0) * mm});
            skLineSegment(sketch, "E41.MirrorCS", {"start": v(120.65, 0) * mm, "end": v(123.83, 0) * mm});
            skLineSegment(sketch, "E42.MirrorCS", {"start": v(146.05, 0) * mm, "end": v(149.23, 0) * mm});
            skLineSegment(sketch, "E43.MirrorCS", {"start": v(44.45, 0) * mm, "end": v(47.63, 0) * mm});
            skLineSegment(sketch, "E44.MirrorCS", {"start": v(241.3, 0) * mm, "end": v(241.3, 6.35) * mm});
            skLineSegment(sketch, "E45.MirrorCS", {"start": v(266.7, 0) * mm, "end": v(266.7, 6.35) * mm});
            skLineSegment(sketch, "E46.MirrorCS", {"start": v(139.7, 0) * mm, "end": v(139.7, 6.35) * mm});
            skLineSegment(sketch, "E47.MirrorCS", {"start": v(165.1, 0) * mm, "end": v(165.1, 6.35) * mm});
            skLineSegment(sketch, "E48.MirrorCS", {"start": v(190.5, 0) * mm, "end": v(190.5, 6.35) * mm});
            skLineSegment(sketch, "E49.MirrorCS", {"start": v(215.9, 0) * mm, "end": v(215.9, 6.35) * mm});
            skLineSegment(sketch, "E50.MirrorCS", {"start": v(63.5, 0) * mm, "end": v(63.5, 6.35) * mm});
            skLineSegment(sketch, "E51.MirrorCS", {"start": v(88.9, 0) * mm, "end": v(88.9, 6.35) * mm});
            skLineSegment(sketch, "E52.MirrorCS", {"start": v(114.3, 0) * mm, "end": v(114.3, 6.35) * mm});
            skLineSegment(sketch, "E53.MirrorCS", {"start": v(139.7, 6.35) * mm, "end": v(142.88, 6.35) * mm});
            skLineSegment(sketch, "E54.MirrorCS", {"start": v(165.1, 6.35) * mm, "end": v(168.28, 6.35) * mm});
            skLineSegment(sketch, "E55.MirrorCS", {"start": v(190.5, 6.35) * mm, "end": v(193.68, 6.35) * mm});
            skLineSegment(sketch, "E56.MirrorCS", {"start": v(215.9, 6.35) * mm, "end": v(219.08, 6.35) * mm});
            skLineSegment(sketch, "E57.MirrorCS", {"start": v(63.5, 6.35) * mm, "end": v(66.68, 6.35) * mm});
            skLineSegment(sketch, "E58.MirrorCS", {"start": v(88.9, 6.35) * mm, "end": v(92.08, 6.35) * mm});
            skLineSegment(sketch, "E59.MirrorCS", {"start": v(114.3, 6.35) * mm, "end": v(117.48, 6.35) * mm});
            skLineSegment(sketch, "E60.MirrorCS", {"start": v(241.3, 0) * mm, "end": v(244.48, 0) * mm});
            skLineSegment(sketch, "E61.MirrorCS", {"start": v(266.7, 0) * mm, "end": v(269.88, 0) * mm});
            skLineSegment(sketch, "E62.MirrorCS", {"start": v(139.7, 0) * mm, "end": v(142.88, 0) * mm});
            skLineSegment(sketch, "E63.MirrorCS", {"start": v(165.1, 0) * mm, "end": v(168.28, 0) * mm});
            skLineSegment(sketch, "E64.MirrorCS", {"start": v(190.5, 0) * mm, "end": v(193.68, 0) * mm});
            skLineSegment(sketch, "E65.MirrorCS", {"start": v(215.9, 0) * mm, "end": v(219.08, 0) * mm});
            skLineSegment(sketch, "E66.MirrorCS", {"start": v(38.1, 0) * mm, "end": v(41.28, 0) * mm});
            skLineSegment(sketch, "E67.MirrorCS", {"start": v(114.3, 0) * mm, "end": v(117.48, 0) * mm});
            skLineSegment(sketch, "E68.MirrorCS", {"start": v(238.13, 0) * mm, "end": v(238.13, 6.35) * mm});
            skLineSegment(sketch, "E69.MirrorCS", {"start": v(263.53, 0) * mm, "end": v(263.53, 6.35) * mm});
            skLineSegment(sketch, "E70.MirrorCS", {"start": v(136.53, 0) * mm, "end": v(136.53, 6.35) * mm});
            skLineSegment(sketch, "E71.MirrorCS", {"start": v(161.93, 0) * mm, "end": v(161.93, 6.35) * mm});
            skLineSegment(sketch, "E72.MirrorCS", {"start": v(187.33, 0) * mm, "end": v(187.33, 6.35) * mm});
            skLineSegment(sketch, "E73.MirrorCS", {"start": v(212.73, 0) * mm, "end": v(212.73, 6.35) * mm});
            skLineSegment(sketch, "E74.MirrorCS", {"start": v(60.33, 0) * mm, "end": v(60.33, 6.35) * mm});
            skLineSegment(sketch, "E75.MirrorCS", {"start": v(85.73, 0) * mm, "end": v(85.73, 6.35) * mm});
            skLineSegment(sketch, "E76.MirrorCS", {"start": v(111.13, 0) * mm, "end": v(111.13, 6.35) * mm});
            skLineSegment(sketch, "E77.MirrorCS", {"start": v(234.95, 0) * mm, "end": v(234.95, 6.35) * mm});
            skLineSegment(sketch, "E78.MirrorCS", {"start": v(260.35, 0) * mm, "end": v(260.35, 6.35) * mm});
            skLineSegment(sketch, "E79.MirrorCS", {"start": v(133.35, 0) * mm, "end": v(133.35, 6.35) * mm});
            skLineSegment(sketch, "E80.MirrorCS", {"start": v(158.75, 0) * mm, "end": v(158.75, 6.35) * mm});
            skLineSegment(sketch, "E81.MirrorCS", {"start": v(184.15, 0) * mm, "end": v(184.15, 6.35) * mm});
            skLineSegment(sketch, "E82.MirrorCS", {"start": v(209.55, 0) * mm, "end": v(209.55, 6.35) * mm});
            skLineSegment(sketch, "E83.MirrorCS", {"start": v(57.15, 0) * mm, "end": v(57.15, 6.35) * mm});
            skLineSegment(sketch, "E84.MirrorCS", {"start": v(82.55, 0) * mm, "end": v(82.55, 6.35) * mm});
            skLineSegment(sketch, "E85.MirrorCS", {"start": v(107.95, 0) * mm, "end": v(107.95, 6.35) * mm});
            skLineSegment(sketch, "E86.MirrorCS", {"start": v(184.15, 6.35) * mm, "end": v(187.33, 6.35) * mm});
            skLineSegment(sketch, "E87.MirrorCS", {"start": v(209.55, 6.35) * mm, "end": v(212.73, 6.35) * mm});
            skLineSegment(sketch, "E88.MirrorCS", {"start": v(82.55, 6.35) * mm, "end": v(85.73, 6.35) * mm});
            skLineSegment(sketch, "E89.MirrorCS", {"start": v(107.95, 6.35) * mm, "end": v(111.13, 6.35) * mm});
            skLineSegment(sketch, "E90.MirrorCS", {"start": v(133.35, 6.35) * mm, "end": v(136.53, 6.35) * mm});
            skLineSegment(sketch, "E91.MirrorCS", {"start": v(158.75, 6.35) * mm, "end": v(161.93, 6.35) * mm});
            skLineSegment(sketch, "E92.MirrorCS", {"start": v(57.15, 6.35) * mm, "end": v(60.33, 6.35) * mm});
            skLineSegment(sketch, "E93.MirrorCS", {"start": v(184.15, 0) * mm, "end": v(187.33, 0) * mm});
            skLineSegment(sketch, "E94.MirrorCS", {"start": v(209.55, 0) * mm, "end": v(212.73, 0) * mm});
            skLineSegment(sketch, "E95.MirrorCS", {"start": v(234.95, 0) * mm, "end": v(238.13, 0) * mm});
            skLineSegment(sketch, "E96.MirrorCS", {"start": v(260.35, 0) * mm, "end": v(263.53, 0) * mm});
            skLineSegment(sketch, "E97.MirrorCS", {"start": v(107.95, 0) * mm, "end": v(111.13, 0) * mm});
            skLineSegment(sketch, "E98.MirrorCS", {"start": v(133.35, 0) * mm, "end": v(136.53, 0) * mm});
            skLineSegment(sketch, "E99.MirrorCS", {"start": v(158.75, 0) * mm, "end": v(161.93, 0) * mm});
            skLineSegment(sketch, "E100.MirrorCS", {"start": v(31.75, 0) * mm, "end": v(34.93, 0) * mm});
            skLineSegment(sketch, "E101.MirrorCS", {"start": v(180.98, 0) * mm, "end": v(180.98, 6.35) * mm});
            skLineSegment(sketch, "E102.MirrorCS", {"start": v(206.38, 0) * mm, "end": v(206.38, 6.35) * mm});
            skLineSegment(sketch, "E103.MirrorCS", {"start": v(231.78, 0) * mm, "end": v(231.78, 6.35) * mm});
            skLineSegment(sketch, "E104.MirrorCS", {"start": v(257.18, 0) * mm, "end": v(257.18, 6.35) * mm});
            skLineSegment(sketch, "E105.MirrorCS", {"start": v(79.38, 0) * mm, "end": v(79.38, 6.35) * mm});
            skLineSegment(sketch, "E106.MirrorCS", {"start": v(104.78, 0) * mm, "end": v(104.78, 6.35) * mm});
            skLineSegment(sketch, "E107.MirrorCS", {"start": v(130.18, 0) * mm, "end": v(130.18, 6.35) * mm});
            skLineSegment(sketch, "E108.MirrorCS", {"start": v(155.58, 0) * mm, "end": v(155.58, 6.35) * mm});
            skLineSegment(sketch, "E109.MirrorCS", {"start": v(53.98, 0) * mm, "end": v(53.98, 6.35) * mm});
            skLineSegment(sketch, "E110.MirrorCS", {"start": v(177.8, 0) * mm, "end": v(177.8, 6.35) * mm});
            skLineSegment(sketch, "E111.MirrorCS", {"start": v(203.2, 0) * mm, "end": v(203.2, 6.35) * mm});
            skLineSegment(sketch, "E112.MirrorCS", {"start": v(228.6, 0) * mm, "end": v(228.6, 6.35) * mm});
            skLineSegment(sketch, "E113.MirrorCS", {"start": v(254, 0) * mm, "end": v(254, 6.35) * mm});
            skLineSegment(sketch, "E114.MirrorCS", {"start": v(76.2, 0) * mm, "end": v(76.2, 6.35) * mm});
            skLineSegment(sketch, "E115.MirrorCS", {"start": v(101.6, 0) * mm, "end": v(101.6, 6.35) * mm});
            skLineSegment(sketch, "E116.MirrorCS", {"start": v(127, 0) * mm, "end": v(127, 6.35) * mm});
            skLineSegment(sketch, "E117.MirrorCS", {"start": v(152.4, 0) * mm, "end": v(152.4, 6.35) * mm});
            skLineSegment(sketch, "E118.MirrorCS", {"start": v(50.8, 0) * mm, "end": v(50.8, 6.35) * mm});
            skLineSegment(sketch, "E119.MirrorCS", {"start": v(76.2, 6.35) * mm, "end": v(79.38, 6.35) * mm});
            skLineSegment(sketch, "E120.MirrorCS", {"start": v(101.6, 6.35) * mm, "end": v(104.78, 6.35) * mm});
            skLineSegment(sketch, "E121.MirrorCS", {"start": v(127, 6.35) * mm, "end": v(130.18, 6.35) * mm});
            skLineSegment(sketch, "E122.MirrorCS", {"start": v(152.4, 6.35) * mm, "end": v(155.58, 6.35) * mm});
            skLineSegment(sketch, "E123.MirrorCS", {"start": v(50.8, 6.35) * mm, "end": v(53.98, 6.35) * mm});
            skLineSegment(sketch, "E124.MirrorCS", {"start": v(177.8, 6.35) * mm, "end": v(180.98, 6.35) * mm});
            skLineSegment(sketch, "E125.MirrorCS", {"start": v(203.2, 6.35) * mm, "end": v(206.38, 6.35) * mm});
            skLineSegment(sketch, "E126.MirrorCS", {"start": v(228.6, 6.35) * mm, "end": v(231.78, 6.35) * mm});
            skLineSegment(sketch, "E127.MirrorCS", {"start": v(177.8, 0) * mm, "end": v(180.98, 0) * mm});
            skLineSegment(sketch, "E128.MirrorCS", {"start": v(203.2, 0) * mm, "end": v(206.38, 0) * mm});
            skLineSegment(sketch, "E129.MirrorCS", {"start": v(228.6, 0) * mm, "end": v(231.78, 0) * mm});
            skLineSegment(sketch, "E130.MirrorCS", {"start": v(254, 0) * mm, "end": v(257.18, 0) * mm});
            skLineSegment(sketch, "E131.MirrorCS", {"start": v(101.6, 0) * mm, "end": v(104.78, 0) * mm});
            skLineSegment(sketch, "E132.MirrorCS", {"start": v(127, 0) * mm, "end": v(130.18, 0) * mm});
            skLineSegment(sketch, "E133.MirrorCS", {"start": v(152.4, 0) * mm, "end": v(155.58, 0) * mm});
            skLineSegment(sketch, "E134.MirrorCS", {"start": v(174.63, 0) * mm, "end": v(174.63, 6.35) * mm});
            skLineSegment(sketch, "E135.MirrorCS", {"start": v(200.03, 0) * mm, "end": v(200.03, 6.35) * mm});
            skLineSegment(sketch, "E136.MirrorCS", {"start": v(225.43, 0) * mm, "end": v(225.43, 6.35) * mm});
            skLineSegment(sketch, "E137.MirrorCS", {"start": v(250.83, 0) * mm, "end": v(250.83, 6.35) * mm});
            skLineSegment(sketch, "E138.MirrorCS", {"start": v(73.03, 0) * mm, "end": v(73.03, 6.35) * mm});
            skLineSegment(sketch, "E139.MirrorCS", {"start": v(98.43, 0) * mm, "end": v(98.43, 6.35) * mm});
            skLineSegment(sketch, "E140.MirrorCS", {"start": v(123.83, 0) * mm, "end": v(123.83, 6.35) * mm});
            skLineSegment(sketch, "E141.MirrorCS", {"start": v(149.23, 0) * mm, "end": v(149.23, 6.35) * mm});
            skLineSegment(sketch, "E142.MirrorCS", {"start": v(120.65, 0) * mm, "end": v(120.65, 6.35) * mm});
            skLineSegment(sketch, "E143.MirrorCS", {"start": v(95.25, 0) * mm, "end": v(95.25, 6.35) * mm});
            skLineSegment(sketch, "E144.MirrorCS", {"start": v(69.85, 0) * mm, "end": v(69.85, 6.35) * mm});
            skLineSegment(sketch, "E145.MirrorCS", {"start": v(247.65, 0) * mm, "end": v(247.65, 6.35) * mm});
            skLineSegment(sketch, "E146.MirrorCS", {"start": v(222.25, 0) * mm, "end": v(222.25, 6.35) * mm});
            skLineSegment(sketch, "E147.MirrorCS", {"start": v(196.85, 0) * mm, "end": v(196.85, 6.35) * mm});
            skLineSegment(sketch, "E148.MirrorCS", {"start": v(171.45, 0) * mm, "end": v(171.45, 6.35) * mm});
            skLineSegment(sketch, "E149.MirrorCS", {"start": v(47.63, 0) * mm, "end": v(47.63, 6.35) * mm});
            skLineSegment(sketch, "E150.MirrorCS", {"start": v(146.05, 0) * mm, "end": v(146.05, 6.35) * mm});
            skLineSegment(sketch, "E151.MirrorCS", {"start": v(44.45, 0) * mm, "end": v(44.45, 6.35) * mm});
            skLineSegment(sketch, "E152.MirrorCS", {"start": v(273.05, 6.35) * mm, "end": v(276.23, 6.35) * mm});
            skLineSegment(sketch, "E153.MirrorCS", {"start": v(247.65, 6.35) * mm, "end": v(250.83, 6.35) * mm});
            skLineSegment(sketch, "E154.MirrorCS", {"start": v(269.88, 0) * mm, "end": v(269.88, 6.35) * mm});
            skLineSegment(sketch, "E155.MirrorCS", {"start": v(41.28, 0) * mm, "end": v(41.28, 6.35) * mm});
            skLineSegment(sketch, "E156.MirrorCS", {"start": v(273.05, 0) * mm, "end": v(276.23, 0) * mm});
            skLineSegment(sketch, "E157.MirrorCS", {"start": v(38.1, 0) * mm, "end": v(38.1, 6.35) * mm});
            skLineSegment(sketch, "E158.MirrorCS", {"start": v(241.3, 6.35) * mm, "end": v(244.48, 6.35) * mm});
            skLineSegment(sketch, "E159.MirrorCS", {"start": v(266.7, 6.35) * mm, "end": v(269.88, 6.35) * mm});
            skLineSegment(sketch, "E160.MirrorCS", {"start": v(38.1, 6.35) * mm, "end": v(41.28, 6.35) * mm});
            skLineSegment(sketch, "E161.MirrorCS", {"start": v(34.93, 0) * mm, "end": v(34.93, 6.35) * mm});
            skLineSegment(sketch, "E162.MirrorCS", {"start": v(31.75, 0) * mm, "end": v(31.75, 6.35) * mm});
            skLineSegment(sketch, "E163.MirrorCS", {"start": v(234.95, 6.35) * mm, "end": v(238.13, 6.35) * mm});
            skLineSegment(sketch, "E164.MirrorCS", {"start": v(260.35, 6.35) * mm, "end": v(263.53, 6.35) * mm});
            skLineSegment(sketch, "E165.MirrorCS", {"start": v(31.75, 6.35) * mm, "end": v(34.93, 6.35) * mm});
            skLineSegment(sketch, "E166.MirrorCS", {"start": v(279.4, 0) * mm, "end": v(279.4, 6.35) * mm});
            skLineSegment(sketch, "E167.MirrorCS", {"start": v(254, 6.35) * mm, "end": v(257.18, 6.35) * mm});
            skLineSegment(sketch, "E168.MirrorCS", {"start": v(25.4, 0) * mm, "end": v(28.58, 0) * mm});
            skLineSegment(sketch, "E169.MirrorCS", {"start": v(279.4, 0) * mm, "end": v(282.58, 0) * mm});
            skLineSegment(sketch, "E170.MirrorCS", {"start": v(276.23, 0) * mm, "end": v(276.23, 6.35) * mm});
            skLineSegment(sketch, "E171.MirrorCS", {"start": v(273.05, 0) * mm, "end": v(273.05, 6.35) * mm});
            skLineSegment(sketch, "E172.MirrorCS", {"start": v(12.7, 0) * mm, "end": v(15.88, 0) * mm});
            skLineSegment(sketch, "E173.MirrorCS", {"start": v(19.05, 0) * mm, "end": v(19.05, 6.35) * mm});
            skLineSegment(sketch, "E174.MirrorCS", {"start": v(19.05, 6.35) * mm, "end": v(22.23, 6.35) * mm});
            skLineSegment(sketch, "E175.MirrorCS", {"start": v(19.05, 0) * mm, "end": v(22.23, 0) * mm});
            skLineSegment(sketch, "E176.MirrorCS", {"start": v(292.1, 0) * mm, "end": v(292.1, 6.35) * mm});
            skLineSegment(sketch, "E177.MirrorCS", {"start": v(292.1, 0) * mm, "end": v(295.28, 0) * mm});
            skLineSegment(sketch, "E178.MirrorCS", {"start": v(288.93, 0) * mm, "end": v(288.93, 6.35) * mm});
            skLineSegment(sketch, "E179.MirrorCS", {"start": v(285.75, 0) * mm, "end": v(285.75, 6.35) * mm});
            skLineSegment(sketch, "E180.MirrorCS", {"start": v(285.75, 6.35) * mm, "end": v(288.93, 6.35) * mm});
            skLineSegment(sketch, "E181.MirrorCS", {"start": v(285.75, 0) * mm, "end": v(288.93, 0) * mm});
            skLineSegment(sketch, "E182.MirrorCS", {"start": v(282.58, 0) * mm, "end": v(282.58, 6.35) * mm});
            skLineSegment(sketch, "E183.MirrorCS", {"start": v(28.58, 0) * mm, "end": v(28.58, 6.35) * mm});
            skLineSegment(sketch, "E184.MirrorCS", {"start": v(25.4, 0) * mm, "end": v(25.4, 6.35) * mm});
            skLineSegment(sketch, "E185.MirrorCS", {"start": v(25.4, 6.35) * mm, "end": v(28.58, 6.35) * mm});
            skLineSegment(sketch, "E186.MirrorCS", {"start": v(279.4, 6.35) * mm, "end": v(282.58, 6.35) * mm});
            skLineSegment(sketch, "E187.MirrorCS", {"start": v(22.23, 0) * mm, "end": v(22.23, 6.35) * mm});
            skLineSegment(sketch, "E188.MirrorCS", {"start": v(295.28, 0) * mm, "end": v(295.28, 6.35) * mm});
            skLineSegment(sketch, "E189.MirrorCS", {"start": v(15.88, 0) * mm, "end": v(15.88, 6.35) * mm});
            skLineSegment(sketch, "E190.MirrorCS", {"start": v(12.7, 0) * mm, "end": v(12.7, 6.35) * mm});
            skLineSegment(sketch, "E191.MirrorCS", {"start": v(12.7, 6.35) * mm, "end": v(15.88, 6.35) * mm});
            skLineSegment(sketch, "E192.MirrorCS", {"start": v(9.53, 0) * mm, "end": v(9.53, 6.35) * mm});
            skLineSegment(sketch, "E193.MirrorCS", {"start": v(6.35, 6.35) * mm, "end": v(9.53, 6.35) * mm});
            skLineSegment(sketch, "E194.MirrorCS", {"start": v(6.35, 0) * mm, "end": v(9.53, 0) * mm});
            skLineSegment(sketch, "E195.MirrorCS", {"start": v(292.1, 6.35) * mm, "end": v(295.28, 6.35) * mm});
            skLineSegment(sketch, "E196.MirrorCS", {"start": v(6.35, 0) * mm, "end": v(6.35, 6.35) * mm});
            skLineSegment(sketch, "E197.MirrorCS", {"start": v(0, 6.35) * mm, "end": v(3.18, 6.35) * mm});
            skLineSegment(sketch, "E198.MirrorCS", {"start": v(0, 0) * mm, "end": v(3.18, 0) * mm});
            skLineSegment(sketch, "E199.MirrorCS", {"start": v(298.45, 0) * mm, "end": v(298.45, 6.35) * mm});
            skLineSegment(sketch, "E200.MirrorCS", {"start": v(298.45, 6.35) * mm, "end": v(301.63, 6.35) * mm});
            skLineSegment(sketch, "E201.MirrorCS", {"start": v(3.18, 0) * mm, "end": v(3.18, 6.35) * mm});
            skLineSegment(sketch, "E202.MirrorCS", {"start": v(0, 0) * mm, "end": v(0, 6.35) * mm});
            skLineSegment(sketch, "E203.MirrorCS", {"start": v(0, 6.35) * mm, "end": v(6.35, 6.35) * mm, "construction": true});
            skLineSegment(sketch, "E204.MirrorCS", {"start": v(301.63, 0) * mm, "end": v(301.63, 6.35) * mm});
            skLineSegment(sketch, "E205.MirrorCS", {"start": v(298.45, 0) * mm, "end": v(301.63, 0) * mm});
            skSolve(sketch);
        }
        {
            var Q0;
            Q0 = qSketchRegion(id + "F4", true);
            extrude(context, id + "F5", {"entities" : qUnion([Q0]), "operationType" : NewBodyOperationType.REMOVE, "endBound" : BoundingType.THROUGH_ALL, "oppositeDirection" : true, "depth" : 25.4 * mm, "offsetDistance" : 25.4 * mm});
        }
        {
            var Q0;
            Q0=makeQuery(id+"F1.opExtrude","CAP_FACE",FACE,{"disambiguationData":[OSD([sQuery(id+"F0.wireOp",EDGE,"E0.bottom"),sQuery(id+"F0.wireOp",EDGE,"E0.top"),sQuery(id+"F0.wireOp",EDGE,"E0.left"),sQuery(id+"F0.wireOp",EDGE,"E0.right"),sQuery(id+"F0.wireOp",EDGE,"E1.bottom"),sQuery(id+"F0.wireOp",EDGE,"E1.top"),sQuery(id+"F0.wireOp",EDGE,"E1.left"),sQuery(id+"F0.wireOp",EDGE,"E1.right")])],"isStart":false});
            var sketch = newSketch(context, id + "F6", { "sketchPlane" : qUnion([Q0])});
            skCircle(sketch, "E206", {"center": v(291.47, 95.25) * mm, "radius": 3.18 * mm});
            skLineSegment(sketch, "E207", {"start": v(273.05, 95.25) * mm, "end": v(304.8, 95.25) * mm, "construction": true});
            skSolve(sketch);
        }
        {
            var Q0;
            Q0 = qSketchRegion(id + "F6", true);
            extrude(context, id + "F7", {"entities" : qUnion([Q0]), "operationType" : NewBodyOperationType.REMOVE, "endBound" : BoundingType.THROUGH_ALL, "oppositeDirection" : true, "depth" : 25.4 * mm, "offsetDistance" : 25.4 * mm});
        }
        {
            var Q0;
            Q0=makeQuery(id+"F1.opExtrude","CAP_FACE",FACE,{"disambiguationData":[OSD([sQuery(id+"F0.wireOp",EDGE,"E0.bottom"),sQuery(id+"F0.wireOp",EDGE,"E0.top"),sQuery(id+"F0.wireOp",EDGE,"E0.left"),sQuery(id+"F0.wireOp",EDGE,"E0.right"),sQuery(id+"F0.wireOp",EDGE,"E1.bottom"),sQuery(id+"F0.wireOp",EDGE,"E1.top"),sQuery(id+"F0.wireOp",EDGE,"E1.left"),sQuery(id+"F0.wireOp",EDGE,"E1.right")])],"isStart":false});
            var sketch = newSketch(context, id + "F8", { "sketchPlane" : qUnion([Q0])});
            skLineSegment(sketch, "E208.bottom", {"start": v(6.35, 158.75) * mm, "end": v(0, 158.75) * mm});
            skLineSegment(sketch, "E208.top", {"start": v(6.35, 31.75) * mm, "end": v(0, 31.75) * mm});
            skLineSegment(sketch, "E208.left", {"start": v(6.35, 158.75) * mm, "end": v(6.35, 31.75) * mm});
            skLineSegment(sketch, "E208.right", {"start": v(0, 158.75) * mm, "end": v(0, 31.75) * mm});
            skSolve(sketch);
        }
        {
            var Q0;
            Q0 = qSketchRegion(id + "F8", true);
            extrude(context, id + "F9", {"entities" : qUnion([Q0]), "operationType" : NewBodyOperationType.REMOVE, "endBound" : BoundingType.THROUGH_ALL, "oppositeDirection" : true, "depth" : 25.4 * mm, "offsetDistance" : 25.4 * mm});
        }
    });
